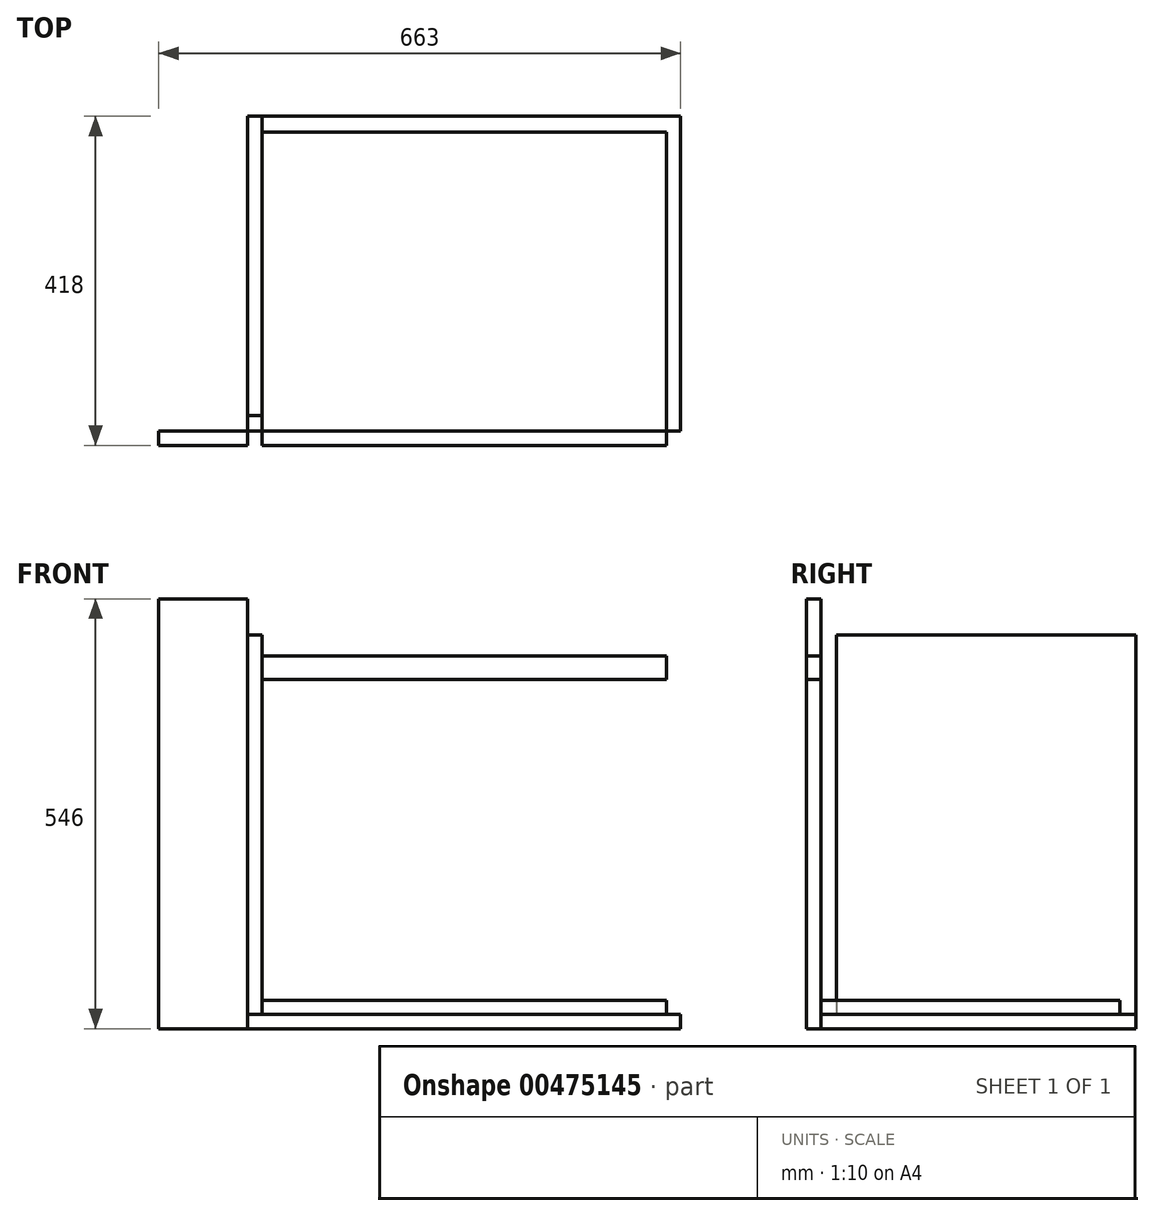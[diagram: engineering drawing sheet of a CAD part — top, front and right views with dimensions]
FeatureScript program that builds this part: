
annotation { "Feature Type Name" : "Feature", "Feature Type Description" : "" }
export const myFeature = defineFeature(function(context is Context, id is Id, definition is map)
    precondition{}
    {
        {
            var Q0;
            Q0=qCreatedBy(makeId("Top.planeOp"),FACE);
            var sketch = newSketch(context, id + "F0", { "sketchPlane" : qUnion([Q0])});
            skLineSegment(sketch, "E0.bottom", {"start": v(0, 0) * mm, "end": v(550, 0) * mm});
            skLineSegment(sketch, "E0.top", {"start": v(0, 400) * mm, "end": v(550, 400) * mm});
            skLineSegment(sketch, "E0.left", {"start": v(0, 0) * mm, "end": v(0, 400) * mm});
            skLineSegment(sketch, "E0.right", {"start": v(550, 0) * mm, "end": v(550, 400) * mm});
            skSolve(sketch);
        }
        {
            var Q0;
            Q0 = qSketchRegion(id + "F0", true);
            extrude(context, id + "F1", {"entities" : qUnion([Q0]), "depth" : 18 * mm});
        }
        {
            var Q0;
            Q0=makeQuery(id+"F1.opExtrude","CAP_FACE",FACE,{"disambiguationData":[OSD([sQuery(id+"F0.wireOp",EDGE,"E0.bottom"),sQuery(id+"F0.wireOp",EDGE,"E0.top"),sQuery(id+"F0.wireOp",EDGE,"E0.left"),sQuery(id+"F0.wireOp",EDGE,"E0.right")])],"isStart":false});
            var sketch = newSketch(context, id + "F2", { "sketchPlane" : qUnion([Q0])});
            skLineSegment(sketch, "E1.bottom", {"start": v(0, 400) * mm, "end": v(18, 400) * mm});
            skLineSegment(sketch, "E1.top", {"start": v(0, 20) * mm, "end": v(18, 20) * mm});
            skLineSegment(sketch, "E1.left", {"start": v(0, 400) * mm, "end": v(0, 20) * mm});
            skLineSegment(sketch, "E1.right", {"start": v(18, 400) * mm, "end": v(18, 20) * mm});
            skSolve(sketch);
        }
        {
            var Q0;
            Q0 = qSketchRegion(id + "F2", true);
            extrude(context, id + "F3", {"entities" : qUnion([Q0]), "depth" : 482 * mm});
        }
        {
            var Q0;
            Q0=qCreatedBy(makeId("Front.planeOp"),FACE);
            var sketch = newSketch(context, id + "F4", { "sketchPlane" : qUnion([Q0])});
            skLineSegment(sketch, "E2.bottom", {"start": v(532, 473.4) * mm, "end": v(18, 473.4) * mm});
            skLineSegment(sketch, "E2.top", {"start": v(532, 443.4) * mm, "end": v(18, 443.4) * mm});
            skLineSegment(sketch, "E2.left", {"start": v(532, 473.4) * mm, "end": v(532, 443.4) * mm});
            skLineSegment(sketch, "E2.right", {"start": v(18, 473.4) * mm, "end": v(18, 443.4) * mm});
            skSolve(sketch);
        }
        {
            var Q0;
            Q0 = qSketchRegion(id + "F4", true);
            extrude(context, id + "F5", {"entities" : qUnion([Q0]), "depth" : 18 * mm});
        }
        {
            var Q0;
            Q0=makeQuery(id+"F1.opExtrude","CAP_FACE",FACE,{"disambiguationData":[OSD([sQuery(id+"F0.wireOp",EDGE,"E0.bottom"),sQuery(id+"F0.wireOp",EDGE,"E0.top"),sQuery(id+"F0.wireOp",EDGE,"E0.left"),sQuery(id+"F0.wireOp",EDGE,"E0.right")])],"isStart":false});
            var sketch = newSketch(context, id + "F6", { "sketchPlane" : qUnion([Q0])});
            skLineSegment(sketch, "E3.bottom", {"start": v(18, 0) * mm, "end": v(532, 0) * mm});
            skLineSegment(sketch, "E3.top", {"start": v(18, 380) * mm, "end": v(532, 380) * mm});
            skLineSegment(sketch, "E3.left", {"start": v(18, 0) * mm, "end": v(18, 380) * mm});
            skLineSegment(sketch, "E3.right", {"start": v(532, 0) * mm, "end": v(532, 380) * mm});
            skSolve(sketch);
        }
        {
            var Q0;
            Q0 = qSketchRegion(id + "F6", true);
            extrude(context, id + "F7", {"entities" : qUnion([Q0]), "depth" : 18 * mm});
        }
        {
            var Q0;
            Q0=qCreatedBy(makeId("Front.planeOp"),FACE);
            var sketch = newSketch(context, id + "F8", { "sketchPlane" : qUnion([Q0])});
            skLineSegment(sketch, "E4.bottom", {"start": v(0, 0) * mm, "end": v(-113, 0) * mm});
            skLineSegment(sketch, "E4.top", {"start": v(0, 546) * mm, "end": v(-113, 546) * mm});
            skLineSegment(sketch, "E4.left", {"start": v(0, 0) * mm, "end": v(0, 546) * mm});
            skLineSegment(sketch, "E4.right", {"start": v(-113, 0) * mm, "end": v(-113, 546) * mm});
            skSolve(sketch);
        }
        {
            var Q0;
            Q0 = qSketchRegion(id + "F8", true);
            extrude(context, id + "F9", {"entities" : qUnion([Q0]), "depth" : 18 * mm});
        }
    });
